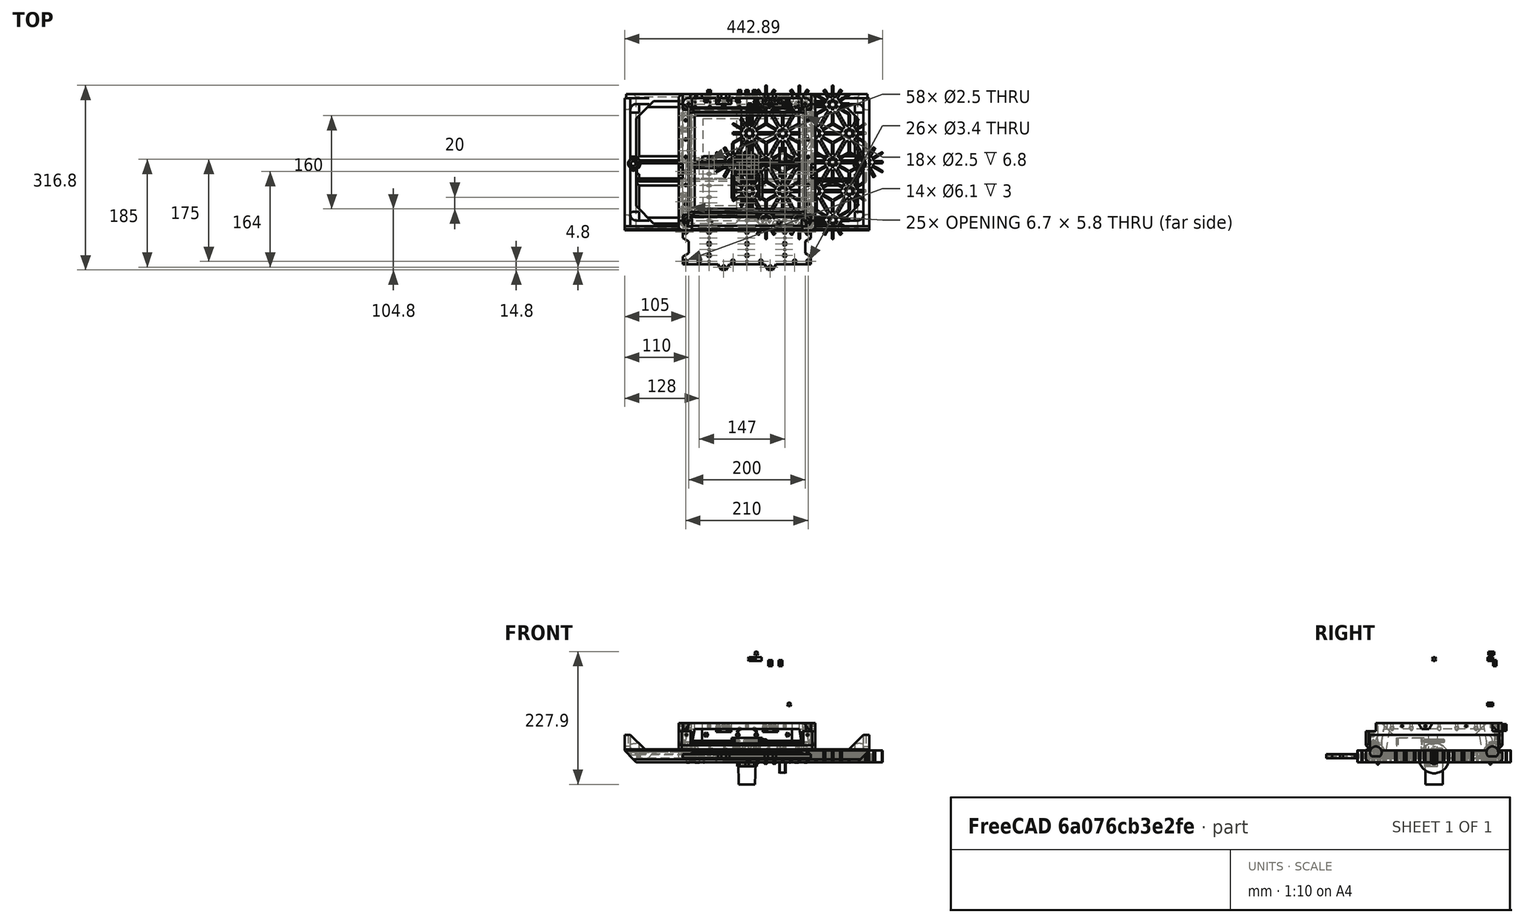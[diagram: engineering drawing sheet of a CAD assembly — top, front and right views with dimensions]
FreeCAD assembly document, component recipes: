
FREECAD ASSEMBLY — COMPONENT RECIPES ("miniXY-Frame")

This assembly document has 23 components, labeled P0..P22 below (a component is one placed body or linked part). 20 of them carry a construction recipe — the FreeCAD feature program that regenerates the part from scratch, quoted from this document or its linked companion documents; the rest are supplied as boundary geometry only. No exploded tour is included for this assembly.
NOTE — document 3 of 3 of this assembly tour. The two overview renders and the header above are repeated from document 1; the component sections below continue where the previous document stopped.
COMPONENT P16 — recipe-attached ("StepperMountRight", modeled in this document).
Construction recipe (the document's own serialized feature program — sketch geometry with constraints, then the solid features built on it; lengths are millimeters unless a unit is written):

FEATURE [PartDesign::CoordinateSystem] LCS_0
  AttacherType = Attacher::AttachEngine3D
  MapMode = 2
  Support = -> [X_Axis039]
FEATURE [Sketcher::SketchObject] Sketch090
  FullyConstrained = true
  MapMode = 5
  Support = -> [XY_Plane039]
  expr: Constraints[62] = -(<<Variables>>.PullyDiameterDrive + <<Variables>>.PullyDiameterIdler) / 2
  expr: Constraints[63] = <<Variables>>.PullyDiameterIdler
  expr: Constraints[84] = <<Variables>>.CavitySpacingX + <<Variables>>.WallThickness
  expr: Constraints[85] = -(<<Variables>>.CavitySpacingY + <<Variables>>.WallThickness)
  expr: Constraints[87] = <<Variables>>.CavitySpacingY + <<Variables>>.WallThickness
  sketch-geometry (33):
    g0: LineSegment StartX=7.34847 StartY=2e-16 StartZ=0 EndX=17 EndY=2e-16 EndZ=0
    g1: LineSegment StartX=17 StartY=2e-16 StartZ=0 EndX=17 EndY=-17 EndZ=0
    g2: LineSegment StartX=18 StartY=-64.5 StartZ=0 EndX=-23.5 EndY=-64.5 EndZ=0
    g3: LineSegment StartX=17 StartY=-17 StartZ=0 EndX=21 EndY=-21 EndZ=0
    g4: LineSegment StartX=21 StartY=-21 StartZ=0 EndX=21 EndY=-61.5 EndZ=0
    g5: Circle CenterX=0 CenterY=-43.5 CenterZ=0 NormalX=0 NormalY=0 NormalZ=1 AngleXU=0 Radius=12.5
    g6: LineSegment StartX=18 StartY=-64.5 StartZ=0 EndX=21 EndY=-61.5 EndZ=0
    g7: LineSegment StartX=-15.5 StartY=-28 StartZ=0 EndX=15.5 EndY=-28 EndZ=0
    g8: LineSegment StartX=15.5 StartY=-28 StartZ=0 EndX=15.5 EndY=-59 EndZ=0
    g9: LineSegment StartX=15.5 StartY=-59 StartZ=0 EndX=-15.5 EndY=-59 EndZ=0
    g10: LineSegment StartX=-15.5 StartY=-59 StartZ=0 EndX=-15.5 EndY=-28 EndZ=0
    g11: Circle CenterX=-15.5 CenterY=-28 CenterZ=0 NormalX=0 NormalY=0 NormalZ=1 AngleXU=0 Radius=1.5
    g12: Circle CenterX=15.5 CenterY=-28 CenterZ=0 NormalX=0 NormalY=0 NormalZ=1 AngleXU=0 Radius=1.5
    g13: Circle CenterX=15.5 CenterY=-59 CenterZ=0 NormalX=0 NormalY=0 NormalZ=1 AngleXU=0 Radius=1.5
    g14: Circle CenterX=-15.5 CenterY=-59 CenterZ=0 NormalX=0 NormalY=0 NormalZ=1 AngleXU=0 Radius=1.5
    g15: LineSegment StartX=-21 StartY=-22.5 StartZ=0 EndX=21 EndY=-22.5 EndZ=0
    g16: LineSegment StartX=21 StartY=-22.5 StartZ=0 EndX=21 EndY=-64.5 EndZ=0
    g17: LineSegment StartX=21 StartY=-64.5 StartZ=0 EndX=-21 EndY=-64.5 EndZ=0
    g18: LineSegment StartX=-21 StartY=-64.5 StartZ=0 EndX=-21 EndY=-22.5 EndZ=0
    g19: LineSegment StartX=-26.5 StartY=64.5 StartZ=0 EndX=-26.5 EndY=-64.5 EndZ=0
    g20: LineSegment StartX=-23 StartY=-17 StartZ=0 EndX=-23 EndY=0 EndZ=0
    g21: LineSegment StartX=-23.5 StartY=-64.5 StartZ=0 EndX=-26.5 EndY=-61.5 EndZ=0
    g22: LineSegment StartX=-26.5 StartY=-61.5 StartZ=0 EndX=-26.5 EndY=-20 EndZ=0
    g23: Circle CenterX=0 CenterY=0 CenterZ=0 NormalX=0 NormalY=0 NormalZ=1 AngleXU=0 Radius=9
    g24: Circle CenterX=-12.73 CenterY=-12.73 CenterZ=0 NormalX=0 NormalY=0 NormalZ=1 AngleXU=0 Radius=9
    g25: Circle CenterX=-12.73 CenterY=-12.73 CenterZ=0 NormalX=0 NormalY=0 NormalZ=1 AngleXU=0 Radius=1.25
    g26: Circle CenterX=0 CenterY=0 CenterZ=0 NormalX=0 NormalY=0 NormalZ=1 AngleXU=0 Radius=1.25
    g27: ArcOfCircle CenterX=0 CenterY=0 CenterZ=0 NormalX=0 NormalY=0 NormalZ=1 AngleXU=0 Radius=6 StartAngle=0.201358 EndAngle=2.94023
    g28: LineSegment StartX=-23 StartY=-9e-16 StartZ=0 EndX=-7.34847 EndY=-9e-16 EndZ=0
    g29: ArcOfCircle CenterX=-7.34847 CenterY=1.5 CenterZ=0 NormalX=0 NormalY=0 NormalZ=1 AngleXU=0 Radius=1.5 StartAngle=4.71239 EndAngle=6.08183
    g30: ArcOfCircle CenterX=7.34847 CenterY=1.5 CenterZ=0 NormalX=0 NormalY=0 NormalZ=1 AngleXU=0 Radius=1.5 StartAngle=3.34295 EndAngle=4.71239
    g31: LineSegment StartX=-26.5 StartY=-20 StartZ=0 EndX=-23.5 EndY=-17 EndZ=0
    g32: LineSegment StartX=-23.5 StartY=-17 StartZ=0 EndX=-23 EndY=-17 EndZ=0
  constraints (89):
    c: Coincident(g0,g1)
    c: Coincident(g2,g21)
    c: Horizontal(g0)
    c: Vertical(g1)
    c: Coincident(g3,g1)
    c: Coincident(g3,g4)
    c: Angle(g3) = -0.785398
    c: PointOnObject(g5,g-2)
    c: Coincident(g4,g6)
    c: Coincident(g2,g6)
    c: Angle(g6) = 0.785398
    c: DistanceX(g2,g4) = 3
    c: Coincident(g7,g8)
    c: Coincident(g8,g9)
    c: Coincident(g9,g10)
    c: Coincident(g10,g7)
    c: Horizontal(g7)
    c: Horizontal(g9)
    c: Vertical(g8)
    c: Vertical(g10)
    c: Symmetric(g7,g8,g5)
    c: Equal(g7,g10)
    c: DistanceY(g10,g10) = 31
    c: Coincident(g11,g7)
    c: Coincident(g12,g7)
    c: Coincident(g13,g8)
    c: Coincident(g14,g9)
    c: Equal(g11,g12)
    c: Equal(g11,g13)
    c: Equal(g11,g14)
    c: Diameter(g11) = 3
    c: Coincident(g15,g16)
    c: Coincident(g16,g17)
    c: Coincident(g17,g18)
    c: Coincident(g18,g15)
    c: Horizontal(g15)
    c: Horizontal(g17)
    c: Vertical(g16)
    c: Vertical(g18)
    c: Symmetric(g15,g16,g5)
    c: Equal(g15,g18)
    c: DistanceY(g18,g18) = 42
    c: PointOnObject(g3,g16)
    c: PointOnObject(g4,g16)
    c: PointOnObject(g2,g17)
    c: PointOnObject(g2,g17)
    c: Symmetric(g19,g19,g-1)
    c: PointOnObject(g19,g17)
    c: DistanceX(g19,g17) = 5.5
    c: Coincident(g32,g20)
    c: Vertical(g20)
    c: Coincident(g22,g31)
    c: Coincident(g21,g22)
    c: Equal(g6,g21)
    c: PointOnObject(g21,g19)
    c: PointOnObject(g31,g19)
    c: Parallel(g3,g21)
    c: Horizontal(g20,g1)
    c: Diameter(g5) = 25
    c: PointOnObject(g23,g-2)
    c: Diameter(g23) = 18
    c: Equal(g23,g24)
    c: DistanceX(g24) = -12.73
    c: DistanceY(g24,g23) = 12.73
    c: Coincident(g25,g24)
    c: Coincident(g26,g23)
    c: Equal(g25,g26)
    c: Diameter(g25) = 2.5
    c: Coincident(g27,g26)
    c: Diameter(g27) = 12
    c: Coincident(g28,g20)
    c: Horizontal(g28)
    c: Diameter(g29) = 3
    c: Tangent(g29,g28) = -1.5708
    c: Tangent(g29,g27) = 1.5708
    c: Diameter(g30) = 3
    c: Tangent(g30,g0) = -1.5708
    c: Tangent(g27,g30) = 1.5708
    c: Coincident(g31,g32)
    c: Horizontal(g32)
    c: Parallel(g6,g31)
    c: Equal(g31,g6)
    c: PointOnObject(g26,g-1)
    c: DistanceX(g20) = -23
    c: DistanceX(g0) = 17
    c: DistanceY(g1) = -17
    c: DistanceY(g15,g1) = 5.5
    c: DistanceY(g1,g1) = 17
    c: Equal(g20,g1)
FEATURE [PartDesign::Pad] Pad034
  Direction = (0,0,1)
  Length = 35
  Length2 = 10
  Profile = -> Sketch090
  ReferenceAxis = -> Sketch090 [N_Axis]
  Type = 0
FEATURE [Sketcher::SketchObject] Sketch091
  AttachmentOffset = pos=(0,0,5) rot=(0,0,1;0rad)
  FullyConstrained = true
  MapMode = 5
  Placement = pos=(0,0,5) rot=(0,0,1;0rad)
  Support = -> [XY_Plane039]
  expr: Constraints[12] = -(Variables.CavitySpacingY + <<Variables>>.WallThickness + 5)
  sketch-geometry (5):
    g0: LineSegment StartX=-21.5 StartY=-22 StartZ=0 EndX=21.5 EndY=-22 EndZ=0
    g1: LineSegment StartX=21.5 StartY=-22 StartZ=0 EndX=21.5 EndY=-65 EndZ=0
    g2: LineSegment StartX=21.5 StartY=-65 StartZ=0 EndX=-21.5 EndY=-65 EndZ=0
    g3: LineSegment StartX=-21.5 StartY=-65 StartZ=0 EndX=-21.5 EndY=-22 EndZ=0
    g4: GeomPoint X=0 Y=-43.5 Z=0
  constraints (13):
    c: Coincident(g0,g1)
    c: Coincident(g1,g2)
    c: Coincident(g2,g3)
    c: Coincident(g3,g0)
    c: Horizontal(g0)
    c: Horizontal(g2)
    c: Vertical(g1)
    c: Vertical(g3)
    c: PointOnObject(g4,g-2)
    c: Symmetric(g0,g1,g4)
    c: Equal(g0,g3)
    c: DistanceY(g3,g3) = 43
    c: DistanceY(g0) = -22
FEATURE [PartDesign::Pocket] Pocket036
  BaseFeature = -> Pad034
  Direction = (0,0,-1)
  Length = 5
  Length2 = 5
  Profile = -> Sketch091
  ReferenceAxis = -> Sketch091 [N_Axis]
  Reversed = true
  Type = 1
FEATURE [Sketcher::SketchObject] Sketch092
  AttachmentOffset = pos=(0,0,14) rot=(0,0,1;0rad)
  FullyConstrained = true
  MapMode = 5
  Placement = pos=(0,0,14) rot=(0,0,1;0rad)
  Support = -> [XY_Plane039]
  expr: Constraints[7] = -(<<Variables>>.CavitySpacingY + <<Variables>>.WallThickness)
  sketch-geometry (4):
    g0: LineSegment StartX=-40 StartY=20 StartZ=0 EndX=40 EndY=20 EndZ=0
    g1: LineSegment StartX=40 StartY=20 StartZ=0 EndX=40 EndY=-17 EndZ=0
    g2: LineSegment StartX=40 StartY=-17 StartZ=0 EndX=-40 EndY=-17 EndZ=0
    g3: LineSegment StartX=-40 StartY=-17 StartZ=0 EndX=-40 EndY=20 EndZ=0
  constraints (10):
    c: Coincident(g0,g1)
    c: Coincident(g1,g2)
    c: Coincident(g2,g3)
    c: Coincident(g3,g0)
    c: Vertical(g3)
    c: Symmetric(g2,g1,g-2)
    c: Symmetric(g0,g0,g-2)
    c: DistanceY(g2) = -17
    c: DistanceY(g0) = 20
    c: DistanceX(g2,g2) = 80
FEATURE [PartDesign::Pocket] Pocket037
  BaseFeature = -> Pocket036
  Direction = (0,0,-1)
  Length = 5
  Length2 = 5
  Profile = -> Sketch092
  ReferenceAxis = -> Sketch092 [N_Axis]
  Reversed = true
  Type = 1
FEATURE [Sketcher::SketchObject] Sketch093
  FullyConstrained = true
  MapMode = 5
  Support = -> [XY_Plane039]
  expr: Constraints[2] = -(Variables.CavitySpacingY - 4)
  sketch-geometry (1):
    g0: Circle CenterX=-10 CenterY=-6 CenterZ=0 NormalX=0 NormalY=0 NormalZ=1 AngleXU=0 Radius=3.5
  constraints (3):
    c: DistanceX(g0) = -10
    c: Diameter(g0) = 7
    c: DistanceY(g0) = -6
FEATURE [PartDesign::Hole] Hole032
  BaseFeature = -> Pocket037
  CustomThreadClearance = 0
  Depth = 25
  DepthType = 0
  Diameter = 3.4
  DrillForDepth = false
  DrillPoint = 1
  DrillPointAngle = 118
  HoleCutCountersinkAngle = 90
  HoleCutCustomValues = false
  HoleCutDepth = 9
  HoleCutDiameter = 6.1
  HoleCutType = 1
  ModelThread = false
  Profile = -> Sketch093
  Reversed = true
  Tapered = false
  TaperedAngle = 90
  ThreadClass = 0
  ThreadDepth = 25
  ThreadDepthType = 0
  ThreadDirection = 0
  ThreadFit = 0
  ThreadSize = 9
  ThreadType = 1
  Threaded = false
  UseCustomThreadClearance = false
FEATURE [PartDesign::SubShapeBinder] Binder
  BindCopyOnChange = 0
  BindMode = 0
  ClaimChildren = false
  Context = -> Part015 [StepperBracketRight.Binder.]
  Fuse = false
  MakeFace = true
  OffsetFill = false
  OffsetIntersection = false
  OffsetJoinType = 0
  OffsetOpenResult = false
  PartialLoad = false
  Placement = pos=(0,0,9) rot=(0,0,1;0rad)
  Relative = true
  Support = -> [Hole032[Sketch093.]]
  _Version = 2
FEATURE [PartDesign::Pad] Pad035
  BaseFeature = -> Hole032
  Direction = (0,0,1)
  Length = 0.1
  Length2 = 10
  Profile = -> Binder
  Type = 0
FEATURE [Sketcher::SketchObject] Sketch098
  AttachmentOffset = pos=(0,0,12) rot=(0,0,1;0rad)
  FullyConstrained = true
  MapMode = 5
  Placement = pos=(0,-12,-2.7e-15) rot=(1,0,0;1.5708rad)
  Support = -> [XZ_Plane039]
  expr: .AttachmentOffset.Base.z = <<Variables>>.WallThickness + 5
  sketch-geometry (3):
    g0: Circle CenterX=5 CenterY=19 CenterZ=0 NormalX=0 NormalY=0 NormalZ=1 AngleXU=0 Radius=3
    g1: Circle CenterX=-18 CenterY=19 CenterZ=0 NormalX=0 NormalY=0 NormalZ=1 AngleXU=0 Radius=3
    g2: LineSegment StartX=-40 StartY=19 StartZ=0 EndX=40 EndY=19 EndZ=0
  constraints (9):
    c: Symmetric(g2,g2,g-2)
    c: DistanceX(g2,g2) = 80
    c: DistanceY(g2) = 19
    c: PointOnObject(g0,g2)
    c: PointOnObject(g1,g2)
    c: Equal(g1,g0)
    c: Diameter(g1) = 6
    c: DistanceX(g0) = 5
    c: DistanceX(g1) = -18
FEATURE [PartDesign::AdditiveCone] Cone
  Angle = 360
  AttacherType = Attacher::AttachEngine3D
  AttachmentOffset = pos=(5,19,17) rot=(1,0,0;3.14159rad)
  BaseFeature = -> Pad035
  Height = 3
  MapMode = 5
  Placement = pos=(5,-17,19) rot=(1,0,0;4.71239rad)
  Radius1 = 3
  Radius2 = 2
  Support = -> [XZ_Plane039]
  expr: .AttachmentOffset.Base.z = <<Variables>>.CavitySpacingY + <<Variables>>.WallThickness
FEATURE [PartDesign::AdditiveCone] Cone001
  Angle = 360
  AttacherType = Attacher::AttachEngine3D
  AttachmentOffset = pos=(-18,19,17) rot=(1,0,0;3.14159rad)
  BaseFeature = -> Cone
  Height = 3
  MapMode = 5
  Placement = pos=(-18,-17,19) rot=(1,0,0;4.71239rad)
  Radius1 = 3
  Radius2 = 2
  Support = -> [XZ_Plane039]
  expr: .AttachmentOffset.Base.z = <<Variables>>.CavitySpacingY + <<Variables>>.WallThickness
FEATURE [PartDesign::Hole] Hole036
  BaseFeature = -> Cone001
  CustomThreadClearance = 0
  Depth = 25
  DepthType = 0
  Diameter = 3.4
  DrillForDepth = false
  DrillPoint = 1
  DrillPointAngle = 118
  HoleCutCountersinkAngle = 90
  HoleCutCustomValues = false
  HoleCutDepth = 3
  HoleCutDiameter = 6.1
  HoleCutType = 1
  ModelThread = false
  Placement = pos=(-18,-17,19) rot=(-1,0,0;1.5708rad)
  Profile = -> Sketch098
  Tapered = false
  TaperedAngle = 90
  ThreadClass = 0
  ThreadDepth = 25
  ThreadDepthType = 0
  ThreadDirection = 0
  ThreadFit = 0
  ThreadSize = 9
  ThreadType = 1
  Threaded = false
  UseCustomThreadClearance = false
FEATURE [PartDesign::Boolean] Boolean006
  BaseFeature = -> Hole036
  Group = -> [Clone076,Clone077]
  Type = 1
FEATURE [PartDesign::Body] StepperBracketRight
  Group = -> [LCS_0,Sketch090,Pad034,Sketch091,Pocket036,Sketch092,Pocket037,Sketch093,Hole032,Binder,Pad035,Cone,Cone001,Sketch098,Hole036,Boolean006]
  Origin = -> Origin039
  Tip = -> Boolean006
COMPONENT P17 — recipe-attached ("UpperBracket", modeled in this document).
Construction recipe (the document's own serialized feature program — sketch geometry with constraints, then the solid features built on it; lengths are millimeters unless a unit is written):

FEATURE [Sketcher::SketchObject] Sketch094
  FullyConstrained = true
  MapMode = 5
  Support = -> [XY_Plane041]
  expr: Constraints[100] = <<Variables>>.FittingGap / 2
  expr: Constraints[101] = <<Variables>>.FittingGap / 2
  expr: Constraints[102] = <<Variables>>.FittingGap / 2
  expr: Constraints[34] = <<Variables>>.PullyDiameterIdler
  expr: Constraints[4] = <<Variables>>.GantorySpacing / 2
  sketch-geometry (40):
    g0: LineSegment StartX=100 StartY=-8.5 StartZ=0 EndX=100 EndY=-1.5 EndZ=0
    g1: LineSegment StartX=26.9 StartY=0 StartZ=0 EndX=26.9 EndY=9 EndZ=0
    g2: LineSegment StartX=20.9 StartY=15 StartZ=0 EndX=9.23 EndY=15 EndZ=0
    g3: LineSegment StartX=7.73 StartY=13.5 StartZ=0 EndX=7.73 EndY=6.5 EndZ=0
    g4: LineSegment StartX=9.23 StartY=5 StartZ=0 EndX=15 EndY=5 EndZ=0
    g5: LineSegment StartX=18 StartY=2 StartZ=0 EndX=18 EndY=-4 EndZ=0
    g6: LineSegment StartX=24 StartY=-10 StartZ=0 EndX=98.5 EndY=-10 EndZ=0
    g7: ArcOfCircle CenterX=15 CenterY=2 CenterZ=0 NormalX=0 NormalY=0 NormalZ=1 AngleXU=0 Radius=3 StartAngle=1e-16 EndAngle=1.5708
    g8: ArcOfCircle CenterX=24 CenterY=-4 CenterZ=0 NormalX=0 NormalY=0 NormalZ=1 AngleXU=0 Radius=6 StartAngle=3.14159 EndAngle=4.71239
    g9: GeomPoint X=18 Y=-10 Z=0
    g10: ArcOfCircle CenterX=9.23 CenterY=13.5 CenterZ=0 NormalX=0 NormalY=0 NormalZ=1 AngleXU=0 Radius=1.5 StartAngle=1.5708 EndAngle=3.14159
    g11: GeomPoint X=7.73 Y=15 Z=0
    g12: ArcOfCircle CenterX=9.23 CenterY=6.5 CenterZ=0 NormalX=0 NormalY=0 NormalZ=1 AngleXU=0 Radius=1.5 StartAngle=3.14159 EndAngle=4.71239
    g13: GeomPoint X=7.73 Y=5 Z=0
    g14: Circle CenterX=12.73 CenterY=10 CenterZ=0 NormalX=0 NormalY=0 NormalZ=1 AngleXU=0 Radius=1.25
    g15: Circle CenterX=24 CenterY=-5 CenterZ=0 NormalX=0 NormalY=0 NormalZ=1 AngleXU=0 Radius=1.25
    g16: Circle CenterX=56 CenterY=-5 CenterZ=0 NormalX=0 NormalY=0 NormalZ=1 AngleXU=0 Radius=1.25
    g17: Circle CenterX=82 CenterY=-5 CenterZ=0 NormalX=0 NormalY=0 NormalZ=1 AngleXU=0 Radius=1.25
    g18: LineSegment StartX=0 StartY=-5 StartZ=0 EndX=100 EndY=-5 EndZ=0
    g19: ArcOfCircle CenterX=20.9 CenterY=9 CenterZ=0 NormalX=0 NormalY=0 NormalZ=1 AngleXU=0 Radius=6 StartAngle=0 EndAngle=1.5708
    g20: GeomPoint X=26.9 Y=15 Z=0
    g21: LineSegment StartX=0 StartY=15 StartZ=0 EndX=100 EndY=15 EndZ=0
    g22: LineSegment StartX=53.1 StartY=0 StartZ=0 EndX=26.9 EndY=0 EndZ=0
    g23: LineSegment StartX=53.1 StartY=7 StartZ=0 EndX=53.1 EndY=0 EndZ=0
    g24: LineSegment StartX=73.9 StartY=10 StartZ=0 EndX=56.1 EndY=10 EndZ=0
    g25: LineSegment StartX=98.5 StartY=0 StartZ=0 EndX=76.9 EndY=0 EndZ=0
    g26: LineSegment StartX=76.9 StartY=0 StartZ=0 EndX=76.9 EndY=7 EndZ=0
    g27: Circle CenterX=65 CenterY=5 CenterZ=0 NormalX=0 NormalY=0 NormalZ=1 AngleXU=0 Radius=1.25
    g28: ArcOfCircle CenterX=56.1 CenterY=7 CenterZ=0 NormalX=0 NormalY=0 NormalZ=1 AngleXU=0 Radius=3 StartAngle=1.5708 EndAngle=3.14159
    g29: GeomPoint X=53.1 Y=10 Z=0
    g30: ArcOfCircle CenterX=73.9 CenterY=7 CenterZ=0 NormalX=0 NormalY=0 NormalZ=1 AngleXU=0 Radius=3 StartAngle=0 EndAngle=1.5708
    g31: GeomPoint X=76.9 Y=10 Z=0
    g32: LineSegment StartX=0 StartY=10 StartZ=0 EndX=100 EndY=10 EndZ=0
    g33: ArcOfCircle CenterX=98.5 CenterY=-1.5 CenterZ=0 NormalX=0 NormalY=0 NormalZ=1 AngleXU=0 Radius=1.5 StartAngle=0 EndAngle=1.5708
    g34: GeomPoint X=100 Y=0 Z=0
    g35: ArcOfCircle CenterX=98.5 CenterY=-8.5 CenterZ=0 NormalX=0 NormalY=0 NormalZ=1 AngleXU=0 Radius=1.5 StartAngle=4.71239 EndAngle=6.28319
    g36: GeomPoint X=100 Y=-10 Z=0
    g37: GeomPoint X=27 Y=15 Z=0
    g38: GeomPoint X=53 Y=15 Z=0
    g39: GeomPoint X=77 Y=15 Z=0
  constraints (103):
    c: Coincident(g22,g1)
    c: Vertical(g1)
    c: PointOnObject(g22,g-1)
    c: Vertical(g0)
    c: DistanceX(g36) = 100
    c: Vertical(g3)
    c: Horizontal(g6)
    c: Horizontal(g4)
    c: Vertical(g5)
    c: Tangent(g4,g7) = 1.5708
    c: Tangent(g7,g5) = 1.5708
    c: Diameter(g7) = 6
    c: DistanceY(g13,g11) = 10
    c: DistanceX(g9) = 18
    c: PointOnObject(g9,g5)
    c: PointOnObject(g9,g6)
    c: Tangent(g5,g8) = -1.5708
    c: Tangent(g6,g8) = -1.5708
    c: PointOnObject(g11,g2)
    c: PointOnObject(g11,g3)
    c: Tangent(g2,g10) = -1.5708
    c: Tangent(g3,g10) = -1.5708
    c: PointOnObject(g13,g3)
    c: PointOnObject(g13,g4)
    c: Tangent(g3,g12) = -1.5708
    c: Tangent(g4,g12) = -1.5708
    c: Diameter(g8) = 12
    c: Equal(g12,g10)
    c: Diameter(g12) = 3
    c: Equal(g14,g15)
    c: Equal(g14,g16)
    c: Equal(g14,g17)
    c: Diameter(g14) = 2.5
    c: DistanceY(g14) = 10
    c: DistanceX(g14) = 12.73
    c: DistanceX(g15) = 24
    c: Horizontal(g18)
    c: PointOnObject(g18,g-2)
    c: PointOnObject(g18,g0)
    c: DistanceY(g18) = -5
    c: PointOnObject(g16,g18)
    c: PointOnObject(g17,g18)
    c: DistanceX(g16) = 56
    c: DistanceX(g17,g34) = 18
    c: DistanceX(g11,g14) = 5
    c: PointOnObject(g20,g2)
    c: PointOnObject(g20,g1)
    c: Tangent(g2,g19) = -1.5708
    c: Tangent(g1,g19) = -1.5708
    c: Equal(g19,g8)
    c: PointOnObject(g21,g-2)
    c: Horizontal(g21)
    c: Equal(g21,g18)
    c: DistanceY(g21) = 15
    c: PointOnObject(g11,g21)
    c: Coincident(g23,g22)
    c: Horizontal(g22)
    c: Coincident(g25,g26)
    c: PointOnObject(g2,g21)
    c: Vertical(g23)
    c: Vertical(g26)
    c: PointOnObject(g25,g-1)
    c: PointOnObject(g34,g-1)
    c: DistanceX(g27) = 65
    c: DistanceY(g27) = 5
    c: Equal(g27,g14)
    c: PointOnObject(g29,g23)
    c: PointOnObject(g29,g24)
    c: Tangent(g23,g28) = -1.5708
    c: Tangent(g24,g28) = -1.5708
    c: PointOnObject(g31,g24)
    c: PointOnObject(g31,g26)
    c: Tangent(g24,g30) = -1.5708
    c: Tangent(g26,g30) = -1.5708
    c: PointOnObject(g32,g-2)
    c: Horizontal(g32)
    c: Equal(g32,g18)
    c: DistanceY(g32) = 10
    c: PointOnObject(g29,g32)
    c: PointOnObject(g31,g32)
    c: Equal(g28,g7)
    c: Equal(g7,g30)
    c: PointOnObject(g34,g25)
    c: PointOnObject(g34,g0)
    c: Tangent(g25,g33) = -1.5708
    c: Tangent(g0,g33) = -1.5708
    c: PointOnObject(g36,g0)
    c: PointOnObject(g36,g6)
    c: Tangent(g0,g35) = -1.5708
    c: Tangent(g6,g35) = -1.5708
    c: Equal(g33,g12)
    c: Equal(g35,g12)
    c: PointOnObject(g15,g18)
    c: PointOnObject(g37,g21)
    c: PointOnObject(g38,g21)
    c: PointOnObject(g39,g21)
    c: DistanceX(g37) = 27
    c: DistanceX(g37,g38) = 26
    c: DistanceX(g39) = 77
    c: DistanceY(g36) = -10
    c: DistanceX(g20,g37) = 0.1
    c: DistanceX(g38,g29) = 0.1
    c: DistanceX(g31,g39) = 0.1
FEATURE [PartDesign::Pad] Pad036
  Direction = (0,0,1)
  Length = 10
  Length2 = 10
  Profile = -> Sketch094
  ReferenceAxis = -> Sketch094 [N_Axis]
  Type = 0
FEATURE [Sketcher::SketchObject] Sketch095
  FullyConstrained = true
  MapMode = 5
  Placement = pos=(0,0,0) rot=(1,0,0;1.5708rad)
  Support = -> [XZ_Plane041]
  expr: Constraints[4] = <<Variables>>.GantorySpacing
  sketch-geometry (9):
    g0: LineSegment StartX=-100 StartY=4 StartZ=0 EndX=100 EndY=4 EndZ=0
    g1: Circle CenterX=32 CenterY=4 CenterZ=0 NormalX=0 NormalY=0 NormalZ=1 AngleXU=0 Radius=1.25
    g2: Circle CenterX=48 CenterY=4 CenterZ=0 NormalX=0 NormalY=0 NormalZ=1 AngleXU=0 Radius=1.25
    g3: Circle CenterX=90 CenterY=4 CenterZ=0 NormalX=0 NormalY=0 NormalZ=1 AngleXU=0 Radius=1.25
    g4: Circle CenterX=-32 CenterY=4 CenterZ=0 NormalX=0 NormalY=0 NormalZ=1 AngleXU=0 Radius=1.25
    g5: Circle CenterX=-48 CenterY=4 CenterZ=0 NormalX=0 NormalY=0 NormalZ=1 AngleXU=0 Radius=1.25
    g6: Circle CenterX=-90 CenterY=4 CenterZ=0 NormalX=0 NormalY=0 NormalZ=1 AngleXU=0 Radius=1.25
    g7: GeomPoint X=-40 Y=4 Z=0
    g8: GeomPoint X=40 Y=4 Z=0
  constraints (16):
    c: PointOnObject(g1,g0)
    c: PointOnObject(g3,g0)
    c: DistanceY(g0) = 4
    c: Symmetric(g0,g0,g-2)
    c: DistanceX(g0,g0) = 200
    c: Symmetric(g4,g1,g-2)
    c: Symmetric(g5,g2,g-2)
    c: Symmetric(g6,g3,g-2)
    c: Equal(g1, g2-g6) x5
    c: Diameter(g1) = 2.5
    c: DistanceX(g1,g2) = 16
    c: PointOnObject(g7,g0)
    c: Symmetric(g7,g8,g-2)
    c: DistanceX(g7,g8) = 80
    c: Symmetric(g1,g2,g8)
    c: DistanceX(g3) = 90
FEATURE [PartDesign::Hole] Hole033
  BaseFeature = -> Pad036
  CustomThreadClearance = 0
  Depth = 25
  DepthType = 0
  Diameter = 2.5
  DrillForDepth = false
  DrillPoint = 1
  DrillPointAngle = 118
  HoleCutCountersinkAngle = 90
  HoleCutCustomValues = false
  HoleCutDepth = 0
  HoleCutDiameter = 6.1
  HoleCutType = 0
  ModelThread = false
  Profile = -> Sketch095
  Reversed = true
  Tapered = false
  TaperedAngle = 90
  ThreadClass = 0
  ThreadDepth = 25
  ThreadDepthType = 0
  ThreadDirection = 0
  ThreadFit = 0
  ThreadSize = 9
  ThreadType = 1
  Threaded = true
  UseCustomThreadClearance = false
FEATURE [Sketcher::SketchObject] Sketch096
  FullyConstrained = true
  MapMode = 5
  Support = -> [XY_Plane041]
  expr: Constraints[29] = <<Variables>>.PullyDiameterDrive + <<Variables>>.PullyDiameterIdler
  sketch-geometry (15):
    g0: LineSegment StartX=9.23 StartY=15 StartZ=0 EndX=16.23 EndY=15 EndZ=0
    g1: LineSegment StartX=17.73 StartY=13.5 StartZ=0 EndX=17.73 EndY=6.5 EndZ=0
    g2: LineSegment StartX=16.23 StartY=5 StartZ=0 EndX=9.23 EndY=5 EndZ=0
    g3: LineSegment StartX=7.73 StartY=6.5 StartZ=0 EndX=7.73 EndY=13.5 EndZ=0
    g4: ArcOfCircle CenterX=9.23 CenterY=13.5 CenterZ=0 NormalX=0 NormalY=0 NormalZ=1 AngleXU=0 Radius=1.5 StartAngle=1.5708 EndAngle=3.14159
    g5: GeomPoint X=7.73 Y=15 Z=0
    g6: ArcOfCircle CenterX=9.23 CenterY=6.5 CenterZ=0 NormalX=0 NormalY=0 NormalZ=1 AngleXU=0 Radius=1.5 StartAngle=3.14159 EndAngle=4.71239
    g7: GeomPoint X=7.73 Y=5 Z=0
    g8: ArcOfCircle CenterX=16.23 CenterY=6.5 CenterZ=0 NormalX=0 NormalY=0 NormalZ=1 AngleXU=0 Radius=1.5 StartAngle=4.71239 EndAngle=6.28319
    g9: GeomPoint X=17.73 Y=5 Z=0
    g10: ArcOfCircle CenterX=16.23 CenterY=13.5 CenterZ=0 NormalX=0 NormalY=0 NormalZ=1 AngleXU=0 Radius=1.5 StartAngle=2e-16 EndAngle=1.5708
    g11: GeomPoint X=17.73 Y=15 Z=0
    g12: GeomPoint X=12.73 Y=10 Z=0
    g13: GeomPoint X=-12.73 Y=10 Z=0
    g14: Circle CenterX=12.73 CenterY=10 CenterZ=0 NormalX=0 NormalY=0 NormalZ=1 AngleXU=0 Radius=1.5
  constraints (32):
    c: Horizontal(g0)
    c: Horizontal(g2)
    c: Vertical(g1)
    c: Vertical(g3)
    c: PointOnObject(g5,g0)
    c: PointOnObject(g5,g3)
    c: Tangent(g0,g4) = 1.5708
    c: Tangent(g3,g4) = 1.5708
    c: PointOnObject(g7,g3)
    c: PointOnObject(g7,g2)
    c: Tangent(g3,g6) = 1.5708
    c: Tangent(g2,g6) = 1.5708
    c: PointOnObject(g9,g2)
    c: PointOnObject(g9,g1)
    c: Tangent(g2,g8) = 1.5708
    c: Tangent(g1,g8) = 1.5708
    c: PointOnObject(g11,g1)
    c: PointOnObject(g11,g0)
    c: Tangent(g1,g10) = 1.5708
    c: Tangent(g0,g10) = 1.5708
    c: Equal(g4,g6)
    c: Equal(g4,g8)
    c: Equal(g4,g10)
    c: Diameter(g4) = 3
    c: Symmetric(g5,g9,g12)
    c: DistanceX(g5,g11) = 10
    c: DistanceY(g7,g5) = 10
    c: DistanceY(g12) = 10
    c: Symmetric(g13,g12,g-2)
    c: DistanceX(g13,g12) = 25.46
    c: Coincident(g14,g12)
    c: Diameter(g14) = 3
FEATURE [PartDesign::Pad] Pad037
  BaseFeature = -> Hole033
  Direction = (0,0,1)
  Length = 17
  Length2 = 10
  Profile = -> Sketch096
  ReferenceAxis = -> Sketch096 [N_Axis]
  Type = 0
FEATURE [PartDesign::Boolean] Boolean007
  BaseFeature = -> Pad037
  Group = -> [Clone078,Clone079,Clone080,Clone081,Clone082,Clone083,Clone084]
  Refine = true
  Type = 1
FEATURE [PartDesign::Body] Body022  label="UpperBracketRightBody"
  Group = -> [Sketch094,Pad036,Sketch095,Hole033,Pad037,Boolean007,Sketch096]
  Origin = -> Origin041
  Tip = -> Boolean007
COMPONENT P18 — recipe-attached ("RightPullyMount", modeled in this document).
Construction recipe (the document's own serialized feature program — sketch geometry with constraints, then the solid features built on it; lengths are millimeters unless a unit is written):

FEATURE [Sketcher::SketchObject] Sketch100
  FullyConstrained = true
  MapMode = 5
  Support = -> [XY_Plane044]
  expr: Constraints[28] = -(<<Variables>>.CavitySpacingX + <<Variables>>.WallThickness)
  expr: Constraints[29] = -(<<Variables>>.CavitySpacingY + <<Variables>>.WallThickness)
  expr: Constraints[30] = <<Variables>>.WallThickness
  expr: Constraints[31] = <<Variables>>.WallThickness + 10
  sketch-geometry (12):
    g0: ArcOfCircle CenterX=0 CenterY=0 CenterZ=0 NormalX=0 NormalY=0 NormalZ=1 AngleXU=0 Radius=6 StartAngle=1e-16 EndAngle=2.94023
    g1: LineSegment StartX=5 StartY=-10 StartZ=0 EndX=5 EndY=-15 EndZ=0
    g2: LineSegment StartX=-12 StartY=-17 StartZ=0 EndX=3 EndY=-17 EndZ=0
    g3: LineSegment StartX=-17 StartY=-12 StartZ=0 EndX=-12 EndY=-17 EndZ=0
    g4: LineSegment StartX=-17 StartY=-12 StartZ=0 EndX=-17 EndY=0 EndZ=0
    g5: LineSegment StartX=6 StartY=7e-16 StartZ=0 EndX=6 EndY=-9 EndZ=0
    g6: ArcOfCircle CenterX=5 CenterY=-9 CenterZ=0 NormalX=0 NormalY=0 NormalZ=1 AngleXU=0 Radius=1 StartAngle=4.71239 EndAngle=6.28319
    g7: ArcOfCircle CenterX=-7.34847 CenterY=1.5 CenterZ=0 NormalX=0 NormalY=0 NormalZ=1 AngleXU=0 Radius=1.5 StartAngle=4.71239 EndAngle=6.08183
    g8: LineSegment StartX=-7.34847 StartY=4e-16 StartZ=0 EndX=-17 EndY=4e-16 EndZ=0
    g9: GeomPoint X=-17 Y=-17 Z=0
    g10: LineSegment StartX=3 StartY=-17 StartZ=0 EndX=5 EndY=-15 EndZ=0
    g11: GeomPoint X=5 Y=-17 Z=0
  constraints (32):
    c: Coincident(g0,g-1)
    c: Diameter(g0) = 12
    c: Angle(g3) = -0.785398
    c: Horizontal(g2)
    c: Vertical(g1)
    c: Vertical(g5)
    c: Horizontal(g8)
    c: Vertical(g4)
    c: Coincident(g2,g3)
    c: Coincident(g6,g1)
    c: PointOnObject(g6,g1)
    c: Tangent(g6,g5) = 1.5708
    c: Tangent(g0,g5) = 1.5708
    c: Tangent(g7,g0) = 1.5708
    c: Tangent(g7,g8) = 1.5708
    c: Coincident(g8,g4)
    c: Coincident(g4,g3)
    c: DistanceX(g3,g2) = 5
    c: PointOnObject(g9,g4)
    c: PointOnObject(g9,g2)
    c: Diameter(g7) = 3
    c: Coincident(g10,g2)
    c: Angle(g10) = 0.785398
    c: Coincident(g10,g1)
    c: PointOnObject(g11,g1)
    c: PointOnObject(g11,g2)
    c: DistanceX(g2,g1) = 2
    c: DistanceX(g11) = 5
    c: DistanceX(g9) = -17
    c: DistanceY(g9) = -17
    c: DistanceY(g11,g1) = 7
    c: DistanceY(g9,g4) = 17
FEATURE [PartDesign::Pad] Pad038
  Direction = (0,0,1)
  Length = 14
  Length2 = 10
  Profile = -> Sketch100
  ReferenceAxis = -> Sketch100 [N_Axis]
  Reversed = true
  Type = 0
FEATURE [Sketcher::SketchObject] Sketch101
  FullyConstrained = true
  MapMode = 5
  Support = -> [XY_Plane043]
  expr: Constraints[12] = -<<Variables>>.CavitySpacingY
  sketch-geometry (8):
    g0: ArcOfCircle CenterX=0 CenterY=0 CenterZ=0 NormalX=0 NormalY=0 NormalZ=1 AngleXU=0 Radius=6 StartAngle=1e-16 EndAngle=1.47976
    g1: ArcOfCircle CenterX=0.5 CenterY=5.47723 CenterZ=0 NormalX=0 NormalY=0 NormalZ=1 AngleXU=0 Radius=0.5 StartAngle=1.47976 EndAngle=3.14159
    g2: ArcOfCircle CenterX=5 CenterY=-9 CenterZ=0 NormalX=0 NormalY=0 NormalZ=1 AngleXU=0 Radius=1 StartAngle=4.71239 EndAngle=6.28319
    g3: LineSegment StartX=0 StartY=-9 StartZ=0 EndX=0 EndY=5.47723 EndZ=0
    g4: LineSegment StartX=6 StartY=7e-16 StartZ=0 EndX=6 EndY=-9 EndZ=0
    g5: LineSegment StartX=1 StartY=-10 StartZ=0 EndX=5 EndY=-10 EndZ=0
    g6: ArcOfCircle CenterX=1 CenterY=-9 CenterZ=0 NormalX=0 NormalY=0 NormalZ=1 AngleXU=0 Radius=1 StartAngle=3.14159 EndAngle=4.71239
    g7: GeomPoint X=0 Y=-10 Z=0
  constraints (20):
    c: Coincident(g0,g-1)
    c: Diameter(g0) = 12
    c: Tangent(g0,g1) = -1.5708
    c: PointOnObject(g7,g-2)
    c: Vertical(g3)
    c: Vertical(g4)
    c: Tangent(g0,g4) = 1.5708
    c: Tangent(g4,g2) = 1.5708
    c: DistanceX(g2) = 5
    c: Tangent(g1,g3) = 1.5708
    c: Diameter(g1) = 1
    c: Coincident(g5,g2)
    c: DistanceY(g2) = -10
    c: Horizontal(g5)
    c: PointOnObject(g7,g5)
    c: PointOnObject(g7,g3)
    c: Tangent(g5,g6) = -1.5708
    c: Tangent(g3,g6) = 1.5708
    c: Diameter(g6) = 2
    c: Vertical(g2,g2)
FEATURE [PartDesign::Pad] Pad039
  BaseFeature = -> Pad038
  Direction = (0,0,1)
  Length = 10
  Length2 = 10
  Profile = -> Sketch101
  ReferenceAxis = -> Sketch101 [N_Axis]
  Type = 0
FEATURE [Sketcher::SketchObject] Sketch102
  FullyConstrained = true
  MapMode = 5
  Placement = pos=(0,0,0) rot=(1,0,0;1.5708rad)
  Support = -> [XZ_Plane044]
  sketch-geometry (5):
    g0: LineSegment StartX=3 StartY=12 StartZ=0 EndX=3 EndY=10 EndZ=0
    g1: LineSegment StartX=3 StartY=10 StartZ=0 EndX=6 EndY=7 EndZ=0
    g2: LineSegment StartX=6 StartY=7 StartZ=0 EndX=8 EndY=7 EndZ=0
    g3: LineSegment StartX=8 StartY=7 StartZ=0 EndX=8 EndY=12 EndZ=0
    g4: LineSegment StartX=8 StartY=12 StartZ=0 EndX=3 EndY=12 EndZ=0
  constraints (15):
    c: Vertical(g0)
    c: Coincident(g0,g1)
    c: Coincident(g1,g2)
    c: Horizontal(g2)
    c: Coincident(g2,g3)
    c: Vertical(g3)
    c: Coincident(g3,g4)
    c: Coincident(g4,g0)
    c: Horizontal(g4)
    c: Angle(g1) = -0.785398
    c: DistanceX(g4,g4) = 5
    c: DistanceY(g3,g3) = 5
    c: DistanceY(g0) = 10
    c: DistanceX(g0,g1) = 3
    c: DistanceX(g1) = 6
FEATURE [PartDesign::Pocket] Pocket039
  BaseFeature = -> Pad039
  Direction = (0,1,2e-16)
  Length = 5
  Length2 = 5
  Midplane = true
  Profile = -> Sketch102
  ReferenceAxis = -> Sketch102 [N_Axis]
  Type = 1
FEATURE [Sketcher::SketchObject] Sketch103
  AttachmentOffset = pos=(0,0,6) rot=(0,0,1;0rad)
  FullyConstrained = true
  MapMode = 5
  Placement = pos=(6,-1.3e-15,1.3e-15) rot=(0.57735,0.57735,0.57735;2.0944rad)
  Support = -> [YZ_Plane044]
  sketch-geometry (1):
    g0: Circle CenterX=0 CenterY=5 CenterZ=0 NormalX=0 NormalY=0 NormalZ=1 AngleXU=0 Radius=1.5
  constraints (3):
    c: PointOnObject(g0,g-2)
    c: DistanceY(g0) = 5
    c: Diameter(g0) = 3
FEATURE [PartDesign::Hole] Hole037
  BaseFeature = -> Pocket039
  CustomThreadClearance = 0
  Depth = 25
  DepthType = 0
  Diameter = 3.4
  DrillForDepth = false
  DrillPoint = 1
  DrillPointAngle = 118
  HoleCutCountersinkAngle = 90
  HoleCutCustomValues = false
  HoleCutDepth = 1
  HoleCutDiameter = 6.1
  HoleCutType = 1
  ModelThread = false
  Profile = -> Sketch103
  Tapered = false
  TaperedAngle = 90
  ThreadClass = 0
  ThreadDepth = 25
  ThreadDepthType = 0
  ThreadDirection = 0
  ThreadFit = 0
  ThreadSize = 9
  ThreadType = 1
  Threaded = false
  UseCustomThreadClearance = false
FEATURE [Sketcher::SketchObject] Sketch104
  AttachmentOffset = pos=(0,0,-5) rot=(0,0,1;0rad)
  FullyConstrained = true
  MapMode = 5
  Placement = pos=(0,0,-5) rot=(0,0,1;0rad)
  Support = -> [XY_Plane044]
  expr: Constraints[0] = -(<<Variables>>.CavitySpacingX - 5)
  expr: Constraints[1] = -<<Variables>>.CavitySpacingY
  sketch-geometry (1):
    g0: Circle CenterX=-5 CenterY=-10 CenterZ=0 NormalX=0 NormalY=0 NormalZ=1 AngleXU=0 Radius=3.05
  constraints (3):
    c: DistanceX(g0) = -5
    c: DistanceY(g0) = -10
    c: Diameter(g0) = 6.1
FEATURE [PartDesign::Hole] Hole038
  BaseFeature = -> Hole037
  CustomThreadClearance = 0
  Depth = 25
  DepthType = 0
  Diameter = 3.4
  DrillForDepth = false
  DrillPoint = 1
  DrillPointAngle = 118
  HoleCutCountersinkAngle = 90
  HoleCutCustomValues = false
  HoleCutDepth = 3.4
  HoleCutDiameter = 6.3
  HoleCutType = 0
  ModelThread = false
  Profile = -> Sketch104
  Reversed = true
  Tapered = false
  TaperedAngle = 90
  ThreadClass = 0
  ThreadDepth = 25
  ThreadDepthType = 0
  ThreadDirection = 0
  ThreadFit = 0
  ThreadSize = 9
  ThreadType = 1
  Threaded = false
  UseCustomThreadClearance = false
FEATURE [Sketcher::SketchObject] Sketch105
  FullyConstrained = true
  MapMode = 5
  Support = -> [XY_Plane044]
  sketch-geometry (1):
    g0: Circle CenterX=0 CenterY=0 CenterZ=0 NormalX=0 NormalY=0 NormalZ=1 AngleXU=0 Radius=1.5
  constraints (2):
    c: Coincident(g0,g-1)
    c: Diameter(g0) = 3
FEATURE [PartDesign::Hole] Hole039
  BaseFeature = -> Hole038
  CustomThreadClearance = 0
  Depth = 25
  DepthType = 0
  Diameter = 2.5
  DrillForDepth = false
  DrillPoint = 1
  DrillPointAngle = 118
  HoleCutCountersinkAngle = 90
  HoleCutCustomValues = false
  HoleCutDepth = 0
  HoleCutDiameter = 6.1
  HoleCutType = 0
  ModelThread = false
  Profile = -> Sketch105
  Tapered = false
  TaperedAngle = 90
  ThreadClass = 0
  ThreadDepth = 25
  ThreadDepthType = 0
  ThreadDirection = 0
  ThreadFit = 0
  ThreadSize = 9
  ThreadType = 1
  Threaded = true
  UseCustomThreadClearance = false
FEATURE [PartDesign::Pocket] Pocket040
  BaseFeature = -> Hole039
  Direction = (0,0,-1)
  Length = 10
  Length2 = 5
  Profile = -> Sketch104
  ReferenceAxis = -> Sketch104 [N_Axis]
  Type = 0
FEATURE [PartDesign::Pad] Pad040
  BaseFeature = -> Pocket040
  Direction = (0,0,1)
  Length = 0.1
  Length2 = 10
  Profile = -> Sketch104
  ReferenceAxis = -> Sketch104 [N_Axis]
  Reversed = true
  Type = 0
FEATURE [PartDesign::Boolean] Boolean008
  BaseFeature = -> Pad040
  Group = -> [Clone085]
  Refine = true
  Type = 1
FEATURE [PartDesign::Body] Body023  label="RightPullyMountBody"
  Group = -> [Sketch100,Pad038,Sketch101,Pad039,Sketch102,Pocket039,Sketch103,Hole037,Sketch104,Hole038,Sketch105,Hole039,Pocket040,Pad040,Boolean008]
  Origin = -> Origin044
  Tip = -> Boolean008
COMPONENT P19 — recipe-attached ("MicroSwitch", modeled in this document).
Construction recipe (the document's own serialized feature program — sketch geometry with constraints, then the solid features built on it; lengths are millimeters unless a unit is written):

FEATURE [Sketcher::SketchObject] Sketch106
  FullyConstrained = true
  MapMode = 5
  Support = -> [XY_Plane046]
  sketch-geometry (8):
    g0: LineSegment StartX=-6.1 StartY=6.5 StartZ=0 EndX=6.1 EndY=6.5 EndZ=0
    g1: LineSegment StartX=6.35 StartY=6.25 StartZ=0 EndX=6.35 EndY=0 EndZ=0
    g2: LineSegment StartX=6.35 StartY=0 StartZ=0 EndX=-6.35 EndY=0 EndZ=0
    g3: LineSegment StartX=-6.35 StartY=0 StartZ=0 EndX=-6.35 EndY=6.25 EndZ=0
    g4: ArcOfCircle CenterX=-6.1 CenterY=6.25 CenterZ=0 NormalX=0 NormalY=0 NormalZ=1 AngleXU=0 Radius=0.25 StartAngle=1.5708 EndAngle=3.14159
    g5: GeomPoint X=-6.35 Y=6.5 Z=0
    g6: ArcOfCircle CenterX=6.1 CenterY=6.25 CenterZ=0 NormalX=0 NormalY=0 NormalZ=1 AngleXU=0 Radius=0.25 StartAngle=7.504e-13 EndAngle=1.5708
    g7: GeomPoint X=6.35 Y=6.5 Z=0
  constraints (18):
    c: Coincident(g1,g2)
    c: Coincident(g2,g3)
    c: Vertical(g3)
    c: PointOnObject(g5,g0)
    c: PointOnObject(g5,g3)
    c: Tangent(g0,g4) = 1.5708
    c: Tangent(g3,g4) = 1.5708
    c: PointOnObject(g7,g0)
    c: PointOnObject(g7,g1)
    c: Tangent(g0,g6) = 1.5708
    c: Tangent(g1,g6) = 1.5708
    c: Symmetric(g7,g5,g-2)
    c: DistanceX(g5,g7) = 12.7
    c: Symmetric(g2,g1,g-2)
    c: PointOnObject(g2,g-1)
    c: Equal(g4,g6)
    c: Diameter(g4) = 0.5
    c: DistanceY(g5) = 6.5
FEATURE [PartDesign::Pad] Pad041
  Direction = (0,0,1)
  Length = 5.7
  Length2 = 10
  Midplane = true
  Profile = -> Sketch106
  ReferenceAxis = -> Sketch106 [N_Axis]
  Type = 0
FEATURE [Sketcher::SketchObject] Sketch107
  FullyConstrained = true
  MapMode = 5
  Support = -> [XY_Plane046]
  sketch-geometry (12):
    g0: LineSegment StartX=-6.4 StartY=0 StartZ=0 EndX=-6.4 EndY=3 EndZ=0
    g1: LineSegment StartX=-6.4 StartY=3 StartZ=0 EndX=-2.75 EndY=3 EndZ=0
    g2: LineSegment StartX=-1.75 StartY=2 StartZ=0 EndX=-1.75 EndY=1 EndZ=0
    g3: LineSegment StartX=-1.75 StartY=1 StartZ=0 EndX=1.75 EndY=1 EndZ=0
    g4: LineSegment StartX=1.75 StartY=1 StartZ=0 EndX=1.75 EndY=2 EndZ=0
    g5: LineSegment StartX=2.75 StartY=3 StartZ=0 EndX=6.4 EndY=3 EndZ=0
    g6: LineSegment StartX=6.4 StartY=3 StartZ=0 EndX=6.4 EndY=0 EndZ=0
    g7: LineSegment StartX=6.4 StartY=0 StartZ=0 EndX=-6.4 EndY=0 EndZ=0
    g8: ArcOfCircle CenterX=-2.75 CenterY=2 CenterZ=0 NormalX=0 NormalY=0 NormalZ=1 AngleXU=0 Radius=1 StartAngle=0 EndAngle=1.5708
    g9: GeomPoint X=-1.75 Y=3 Z=0
    g10: ArcOfCircle CenterX=2.75 CenterY=2 CenterZ=0 NormalX=0 NormalY=0 NormalZ=1 AngleXU=0 Radius=1 StartAngle=1.5708 EndAngle=3.14159
    g11: GeomPoint X=1.75 Y=3 Z=0
  constraints (28):
    c: PointOnObject(g0,g-1)
    c: Vertical(g0)
    c: Coincident(g0,g1)
    c: Horizontal(g1)
    c: Vertical(g2)
    c: Coincident(g2,g3)
    c: Coincident(g3,g4)
    c: Coincident(g5,g6)
    c: Coincident(g6,g7)
    c: Coincident(g7,g0)
    c: Symmetric(g2,g3,g-2)
    c: Symmetric(g0,g6,g-2)
    c: Symmetric(g0,g5,g-2)
    c: PointOnObject(g9,g1)
    c: PointOnObject(g9,g2)
    c: Tangent(g1,g8) = 1.5708
    c: Tangent(g2,g8) = 1.5708
    c: PointOnObject(g11,g5)
    c: PointOnObject(g11,g4)
    c: Tangent(g5,g10) = 1.5708
    c: Tangent(g4,g10) = 1.5708
    c: Symmetric(g9,g11,g-2)
    c: Equal(g8,g10)
    c: Diameter(g8) = 2
    c: DistanceX(g7,g7) = 12.8
    c: DistanceY(g0) = 3
    c: DistanceX(g3,g3) = 3.5
    c: DistanceY(g2) = 1
FEATURE [PartDesign::Pad] Pad042
  BaseFeature = -> Pad041
  Direction = (0,0,1)
  Length = 5.8
  Length2 = 10
  Midplane = true
  Profile = -> Sketch107
  ReferenceAxis = -> Sketch107 [N_Axis]
  Type = 0
FEATURE [Sketcher::SketchObject] Sketch108
  FullyConstrained = true
  MapMode = 5
  Support = -> [XY_Plane047]
  sketch-geometry (1):
    g0: Circle CenterX=-1.95 CenterY=6.4 CenterZ=0 NormalX=0 NormalY=0 NormalZ=1 AngleXU=0 Radius=0.6
  constraints (3):
    c: Diameter(g0) = 1.2
    c: DistanceY(g0) = 6.4
    c: DistanceX(g0) = -1.95
FEATURE [PartDesign::Pad] Pad043
  Direction = (0,0,1)
  Length = 2.9
  Length2 = 10
  Midplane = true
  Profile = -> Sketch108
  ReferenceAxis = -> Sketch108 [N_Axis]
  Type = 0
FEATURE [PartDesign::Body] Body025  label="MicroSwitchButton"
  Group = -> [Sketch108,Pad043]
  Origin = -> Origin047
  Tip = -> Pad043
FEATURE [Sketcher::SketchObject] Sketch109
  FullyConstrained = true
  MapMode = 5
  Support = -> [XY_Plane046]
  sketch-geometry (2):
    g0: Circle CenterX=-3.25 CenterY=1.5 CenterZ=0 NormalX=0 NormalY=0 NormalZ=1 AngleXU=0 Radius=1
    g1: Circle CenterX=3.25 CenterY=1.5 CenterZ=0 NormalX=0 NormalY=0 NormalZ=1 AngleXU=0 Radius=1
  constraints (5):
    c: Symmetric(g0,g1,g-2)
    c: DistanceX(g0,g1) = 6.5
    c: DistanceY(g0) = 1.5
    c: Equal(g0,g1)
    c: Diameter(g0) = 2
FEATURE [PartDesign::Pocket] Pocket041
  BaseFeature = -> Pad042
  Direction = (0,0,-1)
  Length = 5
  Length2 = 5
  Midplane = true
  Profile = -> Sketch109
  ReferenceAxis = -> Sketch109 [N_Axis]
  Type = 1
FEATURE [PartDesign::Body] Body024  label="MicroSwitchBody"
  Group = -> [Sketch106,Pad041,Sketch107,Pad042,Sketch109,Pocket041]
  Origin = -> Origin046
  Tip = -> Pocket041
COMPONENT P20 — recipe-attached ("ZDrive", modeled in this document).
Construction recipe (the document's own serialized feature program — sketch geometry with constraints, then the solid features built on it; lengths are millimeters unless a unit is written):

FEATURE [Sketcher::SketchObject] Sketch117
  FullyConstrained = true
  MapMode = 5
  Support = -> [XY_Plane049]
  expr: Constraints[58] = <<Variables>>.GantorySpacing + <<Variables>>.CavitySpacingX * 2 - 13
  expr: Constraints[61] = <<Variables>>.GantorySpacing - 44
  sketch-geometry (37):
    g0: LineSegment StartX=-103.5 StartY=0 StartZ=0 EndX=-103.5 EndY=-8 EndZ=0
    g1: LineSegment StartX=-89 StartY=-4 StartZ=0 EndX=-89 EndY=-8 EndZ=0
    g2: LineSegment StartX=-89 StartY=-8 StartZ=0 EndX=-81.5 EndY=-8 EndZ=0
    g3: LineSegment StartX=-81.5 StartY=-8 StartZ=0 EndX=-81.5 EndY=-6 EndZ=0
    g4: LineSegment StartX=-81.5 StartY=-6 StartZ=0 EndX=-74.5 EndY=-6 EndZ=0
    g5: LineSegment StartX=-74.5 StartY=-6 StartZ=0 EndX=-74.5 EndY=-8 EndZ=0
    g6: LineSegment StartX=-74.5 StartY=-8 StartZ=0 EndX=-73 EndY=-8 EndZ=0
    g7: LineSegment StartX=-73 StartY=-8 StartZ=0 EndX=-73 EndY=-2.5 EndZ=0
    g8: LineSegment StartX=73 StartY=-2.5 StartZ=0 EndX=73 EndY=-8 EndZ=0
    g9: LineSegment StartX=73 StartY=-8 StartZ=0 EndX=74.5 EndY=-8 EndZ=0
    g10: LineSegment StartX=74.5 StartY=-8 StartZ=0 EndX=74.5 EndY=-6 EndZ=0
    g11: LineSegment StartX=74.5 StartY=-6 StartZ=0 EndX=81.5 EndY=-6 EndZ=0
    g12: LineSegment StartX=81.5 StartY=-6 StartZ=0 EndX=81.5 EndY=-8 EndZ=0
    g13: LineSegment StartX=81.5 StartY=-8 StartZ=0 EndX=89 EndY=-8 EndZ=0
    g14: LineSegment StartX=89 StartY=-8 StartZ=0 EndX=89 EndY=-4 EndZ=0
    g15: LineSegment StartX=103.5 StartY=-8 StartZ=0 EndX=103.5 EndY=0 EndZ=0
    g16: LineSegment StartX=103.5 StartY=0 StartZ=0 EndX=-103.5 EndY=0 EndZ=0
    g17: LineSegment StartX=-103.5 StartY=-8 StartZ=0 EndX=-98.5 EndY=-8 EndZ=0
    g18: LineSegment StartX=-98.5 StartY=-8 StartZ=0 EndX=-98.5 EndY=-4 EndZ=0
    g19: LineSegment StartX=-98.5 StartY=-4 StartZ=0 EndX=-89 EndY=-4 EndZ=0
    g20: LineSegment StartX=89 StartY=-4 StartZ=0 EndX=98.5 EndY=-4 EndZ=0
    g21: LineSegment StartX=98.5 StartY=-4 StartZ=0 EndX=98.5 EndY=-8 EndZ=0
    g22: LineSegment StartX=98.5 StartY=-8 StartZ=0 EndX=103.5 EndY=-8 EndZ=0
    g23: GeomPoint X=0 Y=0 Z=0
    g24: GeomPoint X=-78 Y=-6 Z=0
    g25: GeomPoint X=78 Y=-6 Z=0
    g26: LineSegment StartX=72 StartY=-2.5 StartZ=0 EndX=73 EndY=-2.5 EndZ=0
    g27: LineSegment StartX=72 StartY=-4.5 StartZ=0 EndX=72 EndY=-2.5 EndZ=0
    g28: LineSegment StartX=66.5 StartY=-10 StartZ=0 EndX=72 EndY=-4.5 EndZ=0
    g29: LineSegment StartX=66.5 StartY=-26 StartZ=0 EndX=66.5 EndY=-10 EndZ=0
    g30: LineSegment StartX=65.5 StartY=-25 StartZ=0 EndX=66.5 EndY=-26 EndZ=0
    g31: LineSegment StartX=56.5 StartY=-25 StartZ=0 EndX=65.5 EndY=-25 EndZ=0
    g32: LineSegment StartX=55.5 StartY=-26 StartZ=0 EndX=56.5 EndY=-25 EndZ=0
    g33: LineSegment StartX=55.5 StartY=-6 StartZ=0 EndX=55.5 EndY=-26 EndZ=0
    g34: LineSegment StartX=-73 StartY=-2.5 StartZ=0 EndX=50 EndY=-2.5 EndZ=0
    g35: LineSegment StartX=50 StartY=-2.5 StartZ=0 EndX=50 EndY=-6 EndZ=0
    g36: LineSegment StartX=50 StartY=-6 StartZ=0 EndX=55.5 EndY=-6 EndZ=0
  constraints (93):
    c: Coincident(g0,g17)
    c: Coincident(g19,g1)
    c: Coincident(g1,g2)
    c: Coincident(g2,g3)
    c: Coincident(g3,g4)
    c: Coincident(g4,g5)
    c: Coincident(g5,g6)
    c: Coincident(g6,g7)
    c: Coincident(g7,g34)
    c: Coincident(g26,g8)
    c: Coincident(g8,g9)
    c: Coincident(g9,g10)
    c: Coincident(g10,g11)
    c: Coincident(g11,g12)
    c: Coincident(g12,g13)
    c: Coincident(g13,g14)
    c: Coincident(g14,g20)
    c: Coincident(g22,g15)
    c: Coincident(g15,g16)
    c: Coincident(g16,g0)
    c: Symmetric(g0,g15,g-2)
    c: Symmetric(g0,g22,g-2)
    c: Vertical(g0)
    c: Symmetric(g19,g14,g-2)
    c: Vertical(g1)
    c: Symmetric(g13,g1,g-2)
    c: Horizontal(g2)
    c: Symmetric(g2,g12,g-2)
    c: Symmetric(g3,g11,g-2)
    c: Vertical(g3)
    c: Horizontal(g4)
    c: Symmetric(g4,g10,g-2)
    c: Vertical(g5)
    c: Horizontal(g6)
    c: Vertical(g7)
    c: Symmetric(g5,g9,g-2)
    c: Symmetric(g6,g8,g-2)
    c: Symmetric(g7,g26,g-2)
    c: Coincident(g17,g18)
    c: Horizontal(g17)
    c: Coincident(g18,g19)
    c: Horizontal(g19)
    c: Coincident(g20,g21)
    c: Coincident(g21,g22)
    c: Vertical(g18)
    c: Symmetric(g17,g21,g-2)
    c: Symmetric(g18,g20,g-2)
    c: PointOnObject(g23,g16)
    c: DistanceY(g0,g23) = 8
    c: DistanceY(g1,g23) = 4
    c: DistanceY(g7,g23) = 2.5
    c: DistanceX(g17,g17) = 5
    c: DistanceX(g2,g2) = 7.5
    c: DistanceX(g6,g6) = 1.5
    c: DistanceX(g4,g4) = 7
    c: DistanceY(g1,g23) = 8
    c: DistanceY(g3,g23) = 6
    c: DistanceY(g5,g23) = 8
    c: DistanceX(g16,g16) = 207
    c: Symmetric(g3,g4,g24)
    c: Symmetric(g24,g25,g-2)
    c: DistanceX(g24,g25) = 156
    c: Coincident(g27,g26)
    c: Coincident(g28,g27)
    c: Coincident(g29,g28)
    c: Coincident(g30,g29)
    c: Coincident(g31,g30)
    c: Coincident(g32,g31)
    c: Coincident(g33,g32)
    c: Coincident(g36,g33)
    c: Coincident(g34,g35)
    c: Coincident(g35,g36)
    c: Horizontal(g34)
    c: Vertical(g35)
    c: Horizontal(g36)
    c: Vertical(g33)
    c: Angle(g32) = 0.785398
    c: Angle(g30) = -0.785398
    c: Angle(g28) = 0.785398
    c: Horizontal(g31)
    c: Vertical(g29)
    c: Horizontal(g26)
    c: Vertical(g27)
    c: DistanceY(g35,g23) = 6
    c: DistanceX(g36,g36) = 5.5
    c: DistanceY(g31,g23) = 25
    c: DistanceX(g31,g31) = 9
    c: DistanceX(g32,g31) = 1
    c: DistanceX(g30,g29) = 1
    c: DistanceX(g33,g27) = 16.5
    c: DistanceY(g27,g23) = 4.5
    c: DistanceX(g23,g34) = 50
    c: Coincident(g23,g-1)
FEATURE [PartDesign::Revolution] Revolution001
  Angle = 360
  Axis = (1,0,0)
  Base = (0,0,0)
  Profile = -> Sketch117
  ReferenceAxis = -> Sketch117 [H_Axis]
  Reversed = true
FEATURE [PartDesign::Body] Body026
  Group = -> [Sketch117,Revolution001]
  Origin = -> Origin049
  Tip = -> Revolution001
COMPONENT P21 — recipe-attached ("PrintBed", modeled in this document).
Construction recipe (the document's own serialized feature program — sketch geometry with constraints, then the solid features built on it; lengths are millimeters unless a unit is written):

FEATURE [Sketcher::SketchObject] Sketch118
  FullyConstrained = true
  MapMode = 5
  Support = -> [XY_Plane051]
  sketch-geometry (4):
    g0: LineSegment StartX=-75 StartY=75 StartZ=0 EndX=75 EndY=75 EndZ=0
    g1: LineSegment StartX=75 StartY=75 StartZ=0 EndX=75 EndY=-75 EndZ=0
    g2: LineSegment StartX=75 StartY=-75 StartZ=0 EndX=-75 EndY=-75 EndZ=0
    g3: LineSegment StartX=-75 StartY=-75 StartZ=0 EndX=-75 EndY=75 EndZ=0
  constraints (11):
    c: Coincident(g0,g1)
    c: Coincident(g1,g2)
    c: Coincident(g2,g3)
    c: Coincident(g3,g0)
    c: Horizontal(g0)
    c: Horizontal(g2)
    c: Vertical(g1)
    c: Vertical(g3)
    c: Symmetric(g0,g1,g-1)
    c: Equal(g0,g3)
    c: DistanceY(g3,g3) = 150
FEATURE [PartDesign::Pad] Pad051
  Direction = (0,0,1)
  Length = 7
  Length2 = 10
  Profile = -> Sketch118
  ReferenceAxis = -> Sketch118 [N_Axis]
  Reversed = true
  Type = 0
FEATURE [PartDesign::Body] Body027  label="PrintBedPlate"
  Group = -> [Sketch118,Pad051]
  Origin = -> Origin051
  Tip = -> Pad051
FEATURE [Sketcher::SketchObject] Sketch119
  FullyConstrained = true
  MapMode = 5
  Support = -> [XY_Plane052]
  sketch-geometry (4):
    g0: LineSegment StartX=-60 StartY=60 StartZ=0 EndX=60 EndY=60 EndZ=0
    g1: LineSegment StartX=60 StartY=60 StartZ=0 EndX=60 EndY=-60 EndZ=0
    g2: LineSegment StartX=60 StartY=-60 StartZ=0 EndX=-60 EndY=-60 EndZ=0
    g3: LineSegment StartX=-60 StartY=-60 StartZ=0 EndX=-60 EndY=60 EndZ=0
  constraints (11):
    c: Coincident(g0,g1)
    c: Coincident(g1,g2)
    c: Coincident(g2,g3)
    c: Coincident(g3,g0)
    c: Horizontal(g0)
    c: Horizontal(g2)
    c: Vertical(g1)
    c: Vertical(g3)
    c: Symmetric(g0,g1,g-1)
    c: Equal(g3,g0)
    c: DistanceY(g3,g3) = 120
FEATURE [PartDesign::Pad] Pad052
  Direction = (0,0,1)
  Length = 150
  Length2 = 10
  Profile = -> Sketch119
  ReferenceAxis = -> Sketch119 [N_Axis]
  Reversed = true
  Type = 0
FEATURE [PartDesign::Body] Body028  label="PrintBedBuildVolume"
  Group = -> [Sketch119,Pad052]
  Origin = -> Origin052
  Tip = -> Pad052
FEATURE [Sketcher::SketchObject] Sketch120
  AttachmentOffset = pos=(0,0,-7) rot=(0,0,1;0rad)
  FullyConstrained = true
  MapMode = 5
  Placement = pos=(0,0,-7) rot=(0,0,1;0rad)
  Support = -> [XY_Plane053]
  sketch-geometry (7):
    g0: Circle CenterX=0 CenterY=60 CenterZ=0 NormalX=0 NormalY=0 NormalZ=1 AngleXU=0 Radius=6
    g1: Circle CenterX=-60 CenterY=-60 CenterZ=0 NormalX=0 NormalY=0 NormalZ=1 AngleXU=0 Radius=6
    g2: Circle CenterX=60 CenterY=-60 CenterZ=0 NormalX=0 NormalY=0 NormalZ=1 AngleXU=0 Radius=6
    g3: LineSegment StartX=-75 StartY=75 StartZ=0 EndX=75 EndY=75 EndZ=0
    g4: LineSegment StartX=75 StartY=75 StartZ=0 EndX=75 EndY=-75 EndZ=0
    g5: LineSegment StartX=75 StartY=-75 StartZ=0 EndX=-75 EndY=-75 EndZ=0
    g6: LineSegment StartX=-75 StartY=-75 StartZ=0 EndX=-75 EndY=75 EndZ=0
  constraints (19):
    c: PointOnObject(g0,g-2)
    c: Coincident(g3,g4)
    c: Coincident(g4,g5)
    c: Coincident(g5,g6)
    c: Coincident(g6,g3)
    c: Horizontal(g3)
    c: Horizontal(g5)
    c: Vertical(g4)
    c: Vertical(g6)
    c: Symmetric(g3,g4,g-1)
    c: Equal(g6,g3)
    c: DistanceY(g6,g6) = 150
    c: DistanceY(g0) = 60
    c: Symmetric(g1,g2,g-2)
    c: DistanceY(g1) = -60
    c: DistanceX(g1,g2) = 120
    c: Equal(g0,g1)
    c: Equal(g0,g2)
    c: Diameter(g0) = 12
FEATURE [PartDesign::Body] Body029  label="PrintBedSpacer"
  Group = -> [Sketch120]
  Origin = -> Origin053
COMPONENT P22 — geometry summary ("StepperMountLeft"; no construction recipe available for this part):
  bounding box: 69.9 x 47.5 x 35.0 mm
  tessellated surface: 358 triangles
  volume: 478904856520590275852955231166615715246145621785509215956463249338484086506495282965888048924409776630849818438009607219283139737538738958728098922627072 mm^3 (412191964439279060418985658196402109814164992612279650713553530680162636705680126570253152007688549151859286176115969590900495447564534111069351706624% of its bounding box)
PROVENANCE & LICENSES
A FreeCAD (.FCStd) document from a public repository crawl; recipes are the document's own serialized feature recipes (and, for linked parts, companion documents' recipes).
License: gpl-3.0.
